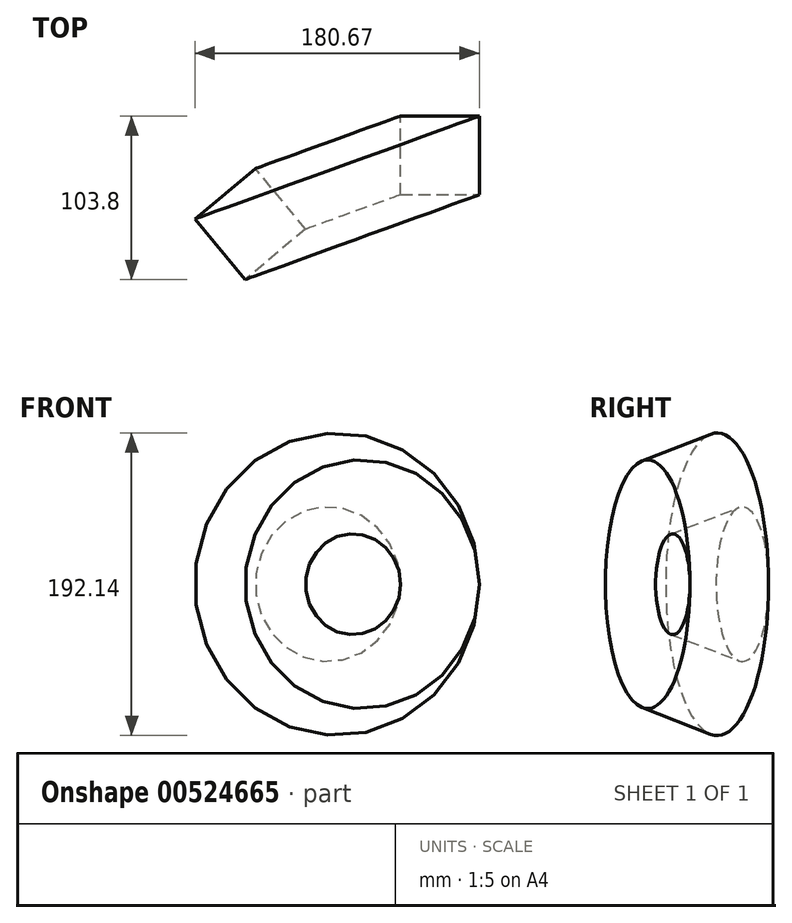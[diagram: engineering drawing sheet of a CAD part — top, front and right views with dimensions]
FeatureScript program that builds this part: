
annotation { "Feature Type Name" : "Feature", "Feature Type Description" : "" }
export const myFeature = defineFeature(function(context is Context, id is Id, definition is map)
    precondition{}
    {
        {
            var Q0;
            Q0=qCreatedBy(makeId("Top.planeOp"),FACE);
            var sketch = newSketch(context, id + "F0", { "sketchPlane" : qUnion([Q0])});
            skLineSegment(sketch, "E0.bottom", {"start": v(0, 0) * mm, "end": v(50, 0) * mm});
            skLineSegment(sketch, "E0.top", {"start": v(0, 50) * mm, "end": v(50, 50) * mm});
            skLineSegment(sketch, "E0.left", {"start": v(0, 0) * mm, "end": v(0, 50) * mm});
            skLineSegment(sketch, "E0.right", {"start": v(50, 0) * mm, "end": v(50, 50) * mm});
            skLineSegment(sketch, "E1", {"start": v(-32.69, -3.82) * mm, "end": v(-55.14, 58.22) * mm, "construction": true});
            skSolve(sketch);
        }
        {
            var Q0;
            Q0=makeQuery(id+"F0.imprint","IMPRINT",FACE,{"disambiguationData":[TD([[makeQuery(id+"F0.imprint","IMPRINT",EDGE,{"derivedFrom":sQuery(id+"F0.wireOp",EDGE,"E0.bottom")}),1.0]])]});
            var Q1;
            Q1=sQuery(id+"F0.wireOp",EDGE,"E1");
            revolve(context, id + "F1", {"entities" : qUnion([Q0]), "axis" : qUnion([Q1]), "revolveType" : RevolveType.FULL});
        }
    });
